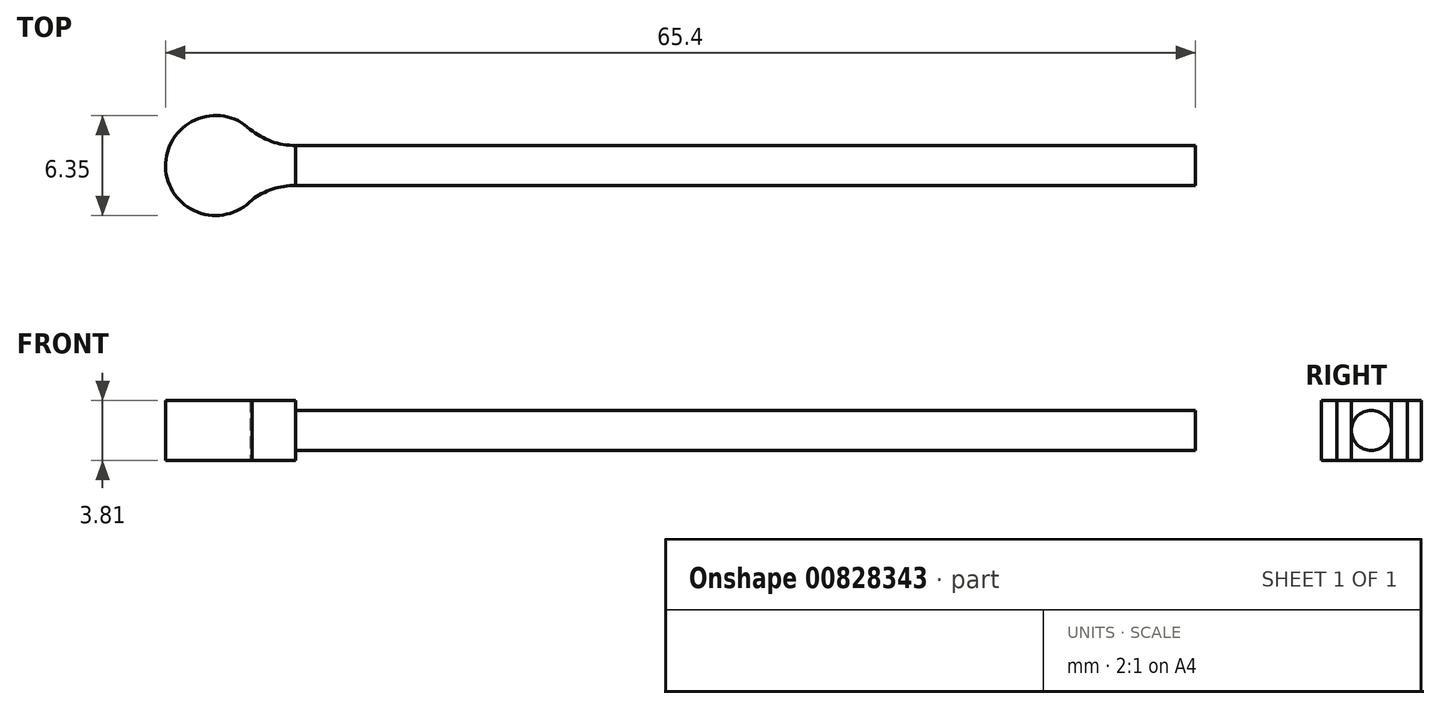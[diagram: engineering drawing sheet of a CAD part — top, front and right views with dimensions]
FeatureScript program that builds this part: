
annotation { "Feature Type Name" : "Feature", "Feature Type Description" : "" }
export const myFeature = defineFeature(function(context is Context, id is Id, definition is map)
    precondition{}
    {
        {
            var Q0;
            Q0=qCreatedBy(makeId("Top.planeOp"),FACE);
            var sketch = newSketch(context, id + "F0", { "sketchPlane" : qUnion([Q0])});
            skArc(sketch, "E0", {"start": v(-2.9, 2.3) * mm, "mid": v(-8.25, -0.09) * mm, "end": v(-2.77, -2.18) * mm});
            skLineSegment(sketch, "E1", {"start": v(0, 1.27) * mm, "end": v(0, -1.27) * mm});
            skArc(sketch, "E2", {"start": v(-2.9, 2.3) * mm, "mid": v(-1.54, 1.54) * mm, "end": v(0, 1.27) * mm});
            skArc(sketch, "E3", {"start": v(0, -1.27) * mm, "mid": v(-1.46, -1.5) * mm, "end": v(-2.77, -2.18) * mm});
            skSolve(sketch);
        }
        {
            var Q0;
            Q0 = qSketchRegion(id + "F0", true);
            extrude(context, id + "F1", {"entities" : qUnion([Q0]), "depth" : 3.8 * mm, "offsetDistance" : 25.4 * mm});
        }
        {
            var Q0;
            Q0=qCreatedBy(makeId("Right.planeOp"),FACE);
            var sketch = newSketch(context, id + "F2", { "sketchPlane" : qUnion([Q0])});
            skCircle(sketch, "E4", {"center": v(0, 1.9) * mm, "radius": 1.27 * mm});
            skSolve(sketch);
        }
        {
            var Q0;
            Q0 = qSketchRegion(id + "F2", true);
            extrude(context, id + "F3", {"entities" : qUnion([Q0]), "operationType" : NewBodyOperationType.ADD, "depth" : 57.15 * mm, "offsetDistance" : 25.4 * mm});
        }
    });
